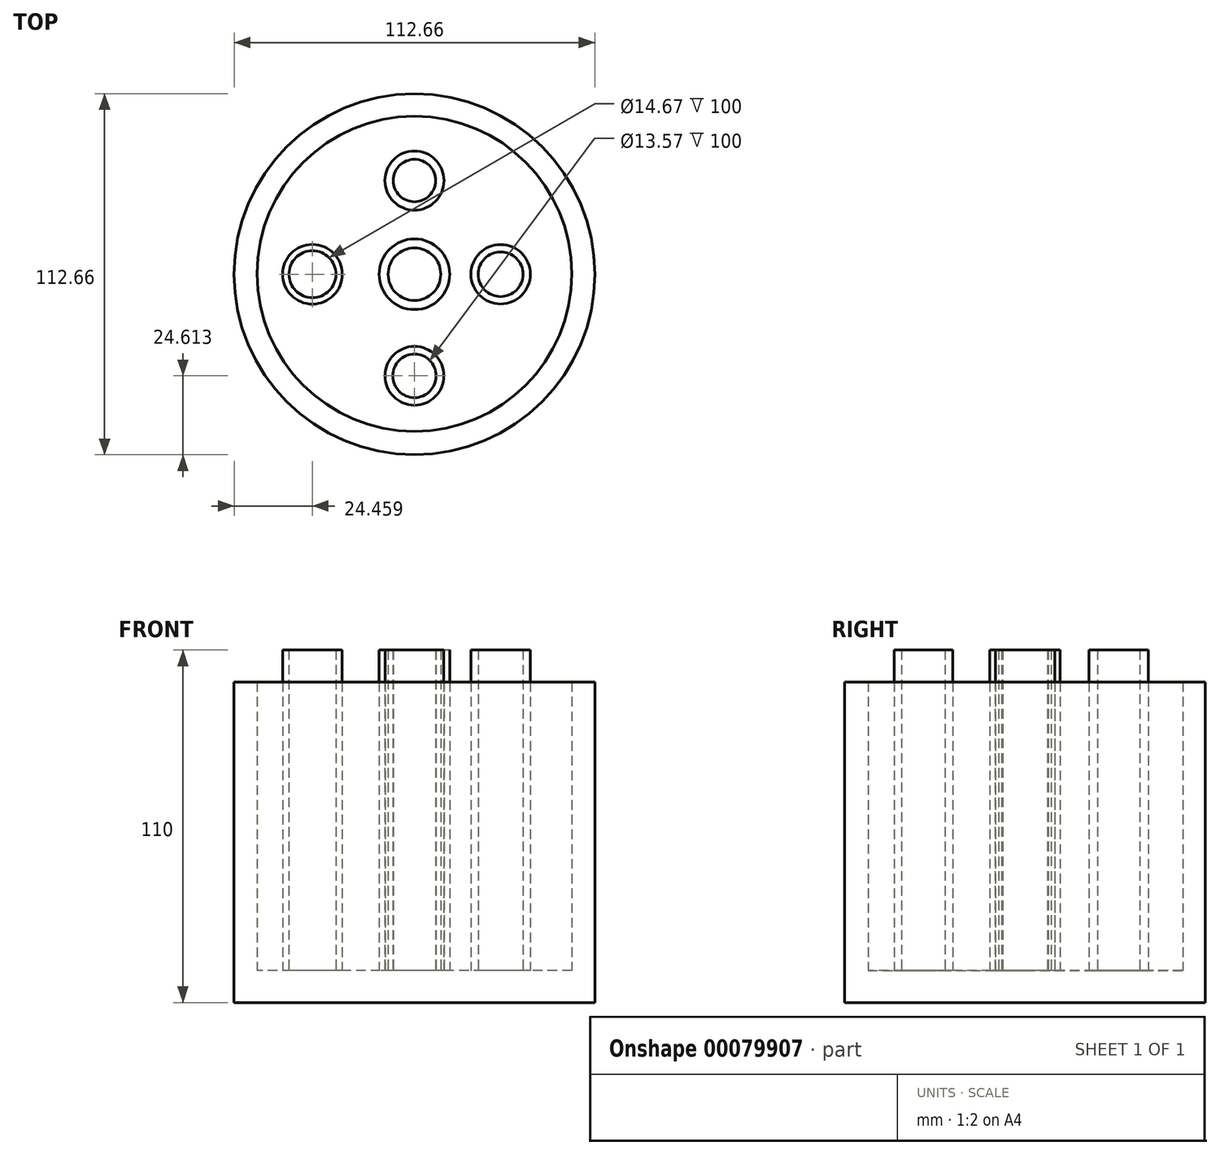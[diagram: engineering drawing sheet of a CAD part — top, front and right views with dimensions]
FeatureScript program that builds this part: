
annotation { "Feature Type Name" : "Feature", "Feature Type Description" : "" }
export const myFeature = defineFeature(function(context is Context, id is Id, definition is map)
    precondition{}
    {
        {
            var Q0;
            Q0=qCreatedBy(makeId("Top.planeOp"),FACE);
            var sketch = newSketch(context, id + "F0", { "sketchPlane" : qUnion([Q0])});
            skCircle(sketch, "E0", {"center": v(0, 0) * mm, "radius": 56.33 * mm});
            skCircle(sketch, "E1", {"center": v(0, 0.15) * mm, "radius": 49.17 * mm});
            skSolve(sketch);
        }
        {
            var Q0;
            Q0=makeQuery(id+"F0.imprint","IMPRINT",FACE,{"disambiguationData":[TD([[makeQuery(id+"F0.imprint","IMPRINT",EDGE,{"derivedFrom":sQuery(id+"F0.wireOp",EDGE,"E0")}),1.0]])]});
            extrude(context, id + "F1", {"entities" : qUnion([Q0]), "depth" : 100 * mm});
        }
        {
            var Q0;
            Q0 = qSketchRegion(id + "F0", true);
            extrude(context, id + "F3", {"entities" : qUnion([Q0]), "operationType" : NewBodyOperationType.ADD, "depth" : 25 * mm});
        }
        {
            var Q0;
            Q0=makeQuery(id+"F0.imprint","IMPRINT",FACE,{"disambiguationData":[TD([[makeQuery(id+"F0.imprint","IMPRINT",EDGE,{"derivedFrom":sQuery(id+"F0.wireOp",EDGE,"E1")}),1.0]])]});
            extrude(context, id + "F4", {"entities" : qUnion([Q0]), "operationType" : NewBodyOperationType.ADD, "depth" : 10 * mm});
        }
        {
            var Q0;
            Q0=makeQuery(id+"F4.opExtrude","CAP_FACE",FACE,{"disambiguationData":[OSD([sQuery(id+"F0.wireOp",EDGE,"E1")])],"isStart":false});
            var sketch = newSketch(context, id + "F5", { "sketchPlane" : qUnion([Q0])});
            skCircle(sketch, "E2", {"center": v(0, 0) * mm, "radius": 8.2 * mm});
            skCircle(sketch, "E3", {"center": v(0, 0) * mm, "radius": 11.03 * mm});
            skCircle(sketch, "E4", {"center": v(0, 29.24) * mm, "radius": 6.62 * mm});
            skCircle(sketch, "E5", {"center": v(0, 29.24) * mm, "radius": 9.23 * mm});
            skCircle(sketch, "E6", {"center": v(26.92, 0) * mm, "radius": 6.99 * mm});
            skCircle(sketch, "E7", {"center": v(26.92, 0) * mm, "radius": 9.28 * mm});
            skCircle(sketch, "E8", {"center": v(-31.87, 0) * mm, "radius": 7.34 * mm});
            skCircle(sketch, "E9", {"center": v(-31.87, 0) * mm, "radius": 9.32 * mm});
            skCircle(sketch, "E10", {"center": v(0, -31.72) * mm, "radius": 6.79 * mm});
            skCircle(sketch, "E11", {"center": v(0, -31.72) * mm, "radius": 9.19 * mm});
            skSolve(sketch);
        }
        {
            var Q0;
            Q0 = qSketchRegion(id + "F5", true);
            extrude(context, id + "F6", {"entities" : qUnion([Q0]), "operationType" : NewBodyOperationType.ADD, "depth" : 100 * mm});
        }
    });
